# Revit family: Strainer-Zurn-Z8746-PC
name_source: partatom
category: Plumbing Fixtures
units: mm (PartAtom-declared; Revit-internal decimal feet)

## family parameters
Cut with Voids When Loaded = No
Host = Face
Maintain Annotation Orientation = No
OmniClass Number = 23.45.55.21
OmniClass Title = Drains (Wastes)
Part Type = Normal
Room Calculation Point = No
Round Connector Dimension = Use Radius
Shared = No

## types (1)
- Z8746-PC (OFFSET LAVATORY STRAINER)
    ADA Compliance = Yes
    Assembly Code = D2010
    CW Connection = No
    CWFU = 0
    Center Distance between Drain & pipe = 5.125 "
    Default Elevation = 48 "
    Description = OFFSET LAVATORY STRAINER
    Drain Material = Chrome-Plated Brass - Zurn - Polished
    HW Connection = No
    HWFU = 0
    Height of Pipe = 8.75 "
    Manufacturer = Zurn
    Manufacturer Brand = Zurn Water, LLC
    Model = Z8746-PC
    Modified Date = 03/27/2026
    Outlet Connection Size (inch) = 1.25 "
    Pipe Material = Steel - Zurn - Zinc Coated
    Product Documentation Link = https://files.zurn.com
    Product Page URL = https://www.zurn.com
    Product data URL = https://bimobject.com
    URL = https://www.zurn.com
    Vent Connection = No
    WFU = 1
    Waste Connection = Yes
    Width of Drain = 2.25 "
    Width of pipe size = 1.25 "

## geometry (parser evidence)
native form markers: Sweep x4
no freeform markers — native parametric forms only
